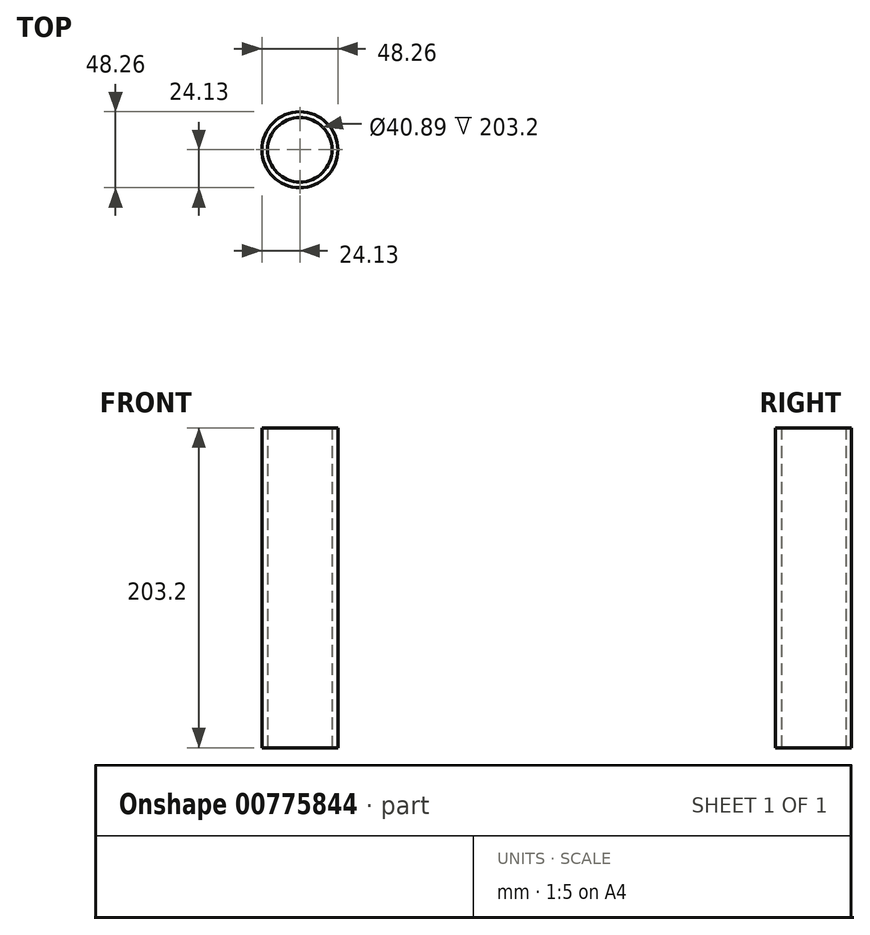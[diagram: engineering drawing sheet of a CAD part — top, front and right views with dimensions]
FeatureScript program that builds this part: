
annotation { "Feature Type Name" : "Feature", "Feature Type Description" : "" }
export const myFeature = defineFeature(function(context is Context, id is Id, definition is map)
    precondition{}
    {
        {
            var Q0;
            Q0=qCreatedBy(makeId("Top.planeOp"),FACE);
            var sketch = newSketch(context, id + "F0", { "sketchPlane" : qUnion([Q0])});
            skCircle(sketch, "E0", {"center": v(0, 0) * mm, "radius": 24.13 * mm});
            skCircle(sketch, "E1", {"center": v(0, 0) * mm, "radius": 20.45 * mm});
            skSolve(sketch);
        }
        {
            var Q0;
            Q0=makeQuery(id+"F0.imprint","IMPRINT",FACE,{"disambiguationData":[TD([[makeQuery(id+"F0.imprint","IMPRINT",EDGE,{"derivedFrom":sQuery(id+"F0.wireOp",EDGE,"E0")}),1.0]])]});
            extrude(context, id + "F1", {"entities" : qUnion([Q0]), "depth" : 203.2 * mm, "offsetDistance" : 25.4 * mm});
        }
    });
